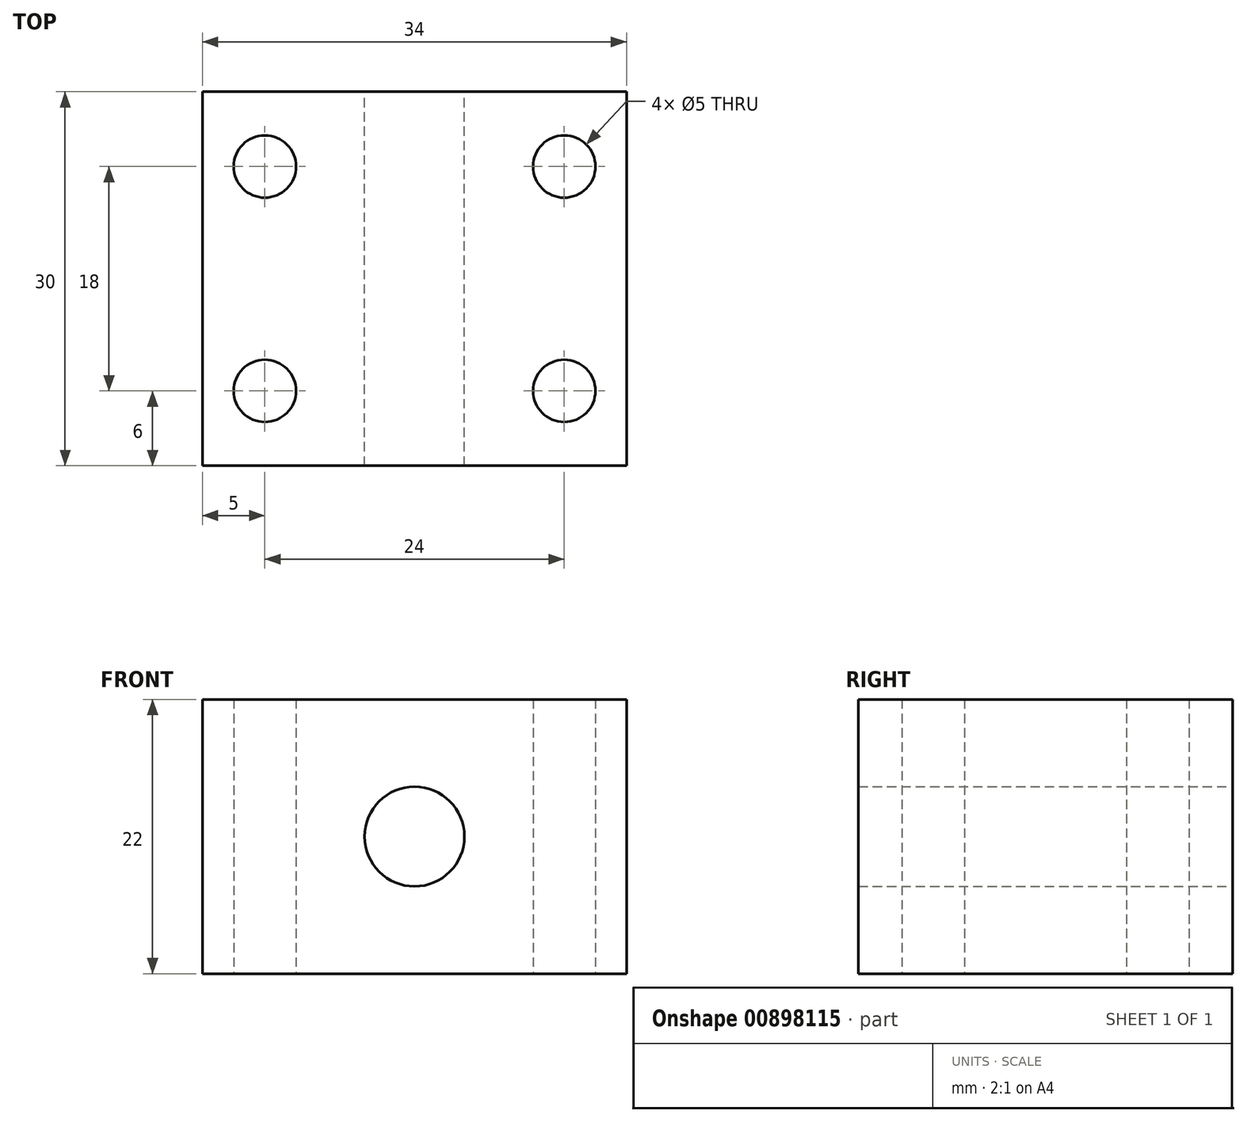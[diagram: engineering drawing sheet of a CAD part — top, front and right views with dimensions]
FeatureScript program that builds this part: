
annotation { "Feature Type Name" : "Feature", "Feature Type Description" : "" }
export const myFeature = defineFeature(function(context is Context, id is Id, definition is map)
    precondition{}
    {
        {
            var Q0;
            Q0=qCreatedBy(makeId("Front.planeOp"),FACE);
            var sketch = newSketch(context, id + "F0", { "sketchPlane" : qUnion([Q0])});
            skLineSegment(sketch, "E0", {"start": v(-17, 0) * mm, "end": v(0, 0) * mm});
            skLineSegment(sketch, "E1", {"start": v(0, 0) * mm, "end": v(17, 0) * mm});
            skLineSegment(sketch, "E2", {"start": v(17, 0) * mm, "end": v(17, 11) * mm});
            skLineSegment(sketch, "E3", {"start": v(17, 11) * mm, "end": v(17, 22) * mm});
            skLineSegment(sketch, "E4", {"start": v(17, 22) * mm, "end": v(7.34, 22) * mm});
            skLineSegment(sketch, "E5", {"start": v(7.34, 22) * mm, "end": v(0, 22) * mm});
            skLineSegment(sketch, "E6", {"start": v(0, 22) * mm, "end": v(-17, 22) * mm});
            skLineSegment(sketch, "E7", {"start": v(-17, 22) * mm, "end": v(-17, 11) * mm});
            skLineSegment(sketch, "E8", {"start": v(-17, 11) * mm, "end": v(-17, 0) * mm});
            skCircle(sketch, "E9", {"center": v(0, 11) * mm, "radius": 4 * mm});
            skLineSegment(sketch, "E10", {"start": v(-17, 11) * mm, "end": v(17, 11) * mm});
            skSolve(sketch);
        }
        {
            var Q0;
            Q0=qCreatedBy(makeId("Top.planeOp"),FACE);
            var sketch = newSketch(context, id + "F1", { "sketchPlane" : qUnion([Q0])});
            skPoint(sketch, "E11", {"position": v(-12, -6) * mm});
            skCircle(sketch, "E12", {"center": v(-12, -6) * mm, "radius": 2 * mm});
            skPoint(sketch, "E13.0.1.0", {"position": v(-12, -24) * mm});
            skCircle(sketch, "E13.0.1.1", {"center": v(-12, -24) * mm, "radius": 2 * mm});
            skPoint(sketch, "E13.1.0.0", {"position": v(12, -6) * mm});
            skCircle(sketch, "E13.1.0.1", {"center": v(12, -6) * mm, "radius": 2 * mm});
            skPoint(sketch, "E13.1.1.0", {"position": v(12, -24) * mm});
            skCircle(sketch, "E13.1.1.1", {"center": v(12, -24) * mm, "radius": 2 * mm});
            skLineSegment(sketch, "E13.direction1", {"start": v(-12, -6) * mm, "end": v(12, -6) * mm, "construction": true});
            skLineSegment(sketch, "E13.direction2", {"start": v(-12, -6) * mm, "end": v(-12, -24) * mm, "construction": true});
            skSolve(sketch);
        }
        {
            var Q0;
            {var subQ0=sQuery(id+"F0.wireOp",EDGE,"E3");Q0=makeQuery(id+"F0.imprint","IMPRINT",FACE,{"disambiguationData":[TD([[makeQuery(id+"F0.imprint","IMPRINT",EDGE,{"derivedFrom":subQ0}),1.0]])]});}
            var Q1;
            Q1=makeQuery(id+"F0.imprint","IMPRINT",FACE,{"disambiguationData":[TD([[makeQuery(id+"F0.imprint","IMPRINT",EDGE,{"derivedFrom":sQuery(id+"F0.wireOp",EDGE,"E0")}),1.0]])]});
            extrude(context, id + "F2", {"entities" : qUnion([Q0, Q1]), "depth" : 30 * mm, "offsetDistance" : 25 * mm});
        }
        {
            var Q0;
            Q0=sQuery(id+"F1.wireOp",VERTEX,"E13.0.1.0");
            var Q1;
            Q1=sQuery(id+"F1.wireOp",VERTEX,"E11");
            var Q2;
            Q2=sQuery(id+"F1.wireOp",VERTEX,"E13.1.1.0");
            var Q3;
            Q3=sQuery(id+"F1.wireOp",VERTEX,"E13.1.0.0");
            var Q4;
            Q4=makeQuery(id+"F2.opExtrude","SWEPT_BODY",BODY,{"disambiguationData":[OSD([sQuery(id+"F0.wireOp",EDGE,"E0"),sQuery(id+"F0.wireOp",EDGE,"E1"),sQuery(id+"F0.wireOp",EDGE,"E2"),sQuery(id+"F0.wireOp",EDGE,"E3"),sQuery(id+"F0.wireOp",EDGE,"E4"),sQuery(id+"F0.wireOp",EDGE,"E5"),sQuery(id+"F0.wireOp",EDGE,"E6"),sQuery(id+"F0.wireOp",EDGE,"E7"),sQuery(id+"F0.wireOp",EDGE,"E8"),sQuery(id+"F0.wireOp",EDGE,"E9")])]});
            hole(context, id + "F3", {"style" : HoleStyle.SIMPLE, "endStyle" : HoleEndStyle.BLIND, "oppositeDirection" : true, "holeDiameter" : 5 * mm, "majorDiameter" : 5 * mm, "holeDepth" : 22 * mm, "isTappedThrough" : true, "tappedDepth" : 12 * mm, "tapClearance" : 3, "locations" : qUnion([Q0, Q1, Q2, Q3]), "scope" : qUnion([Q4])});
        }
    });
